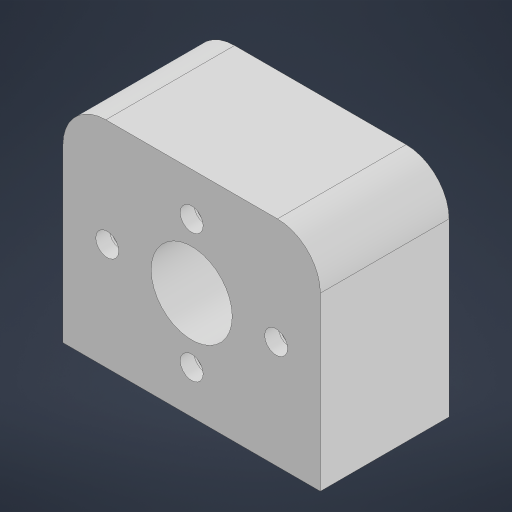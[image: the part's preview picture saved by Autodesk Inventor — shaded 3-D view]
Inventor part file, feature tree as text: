
AUTODESK INVENTOR PART (.ipt)
format: ipt  version: 2023 (Build 270158000, 158)  size: 222,720 bytes
history: native  units: in
note: dims shown in document units (in); Inventor stores cm internally (conversion verified against a paired STEP export)
features: sketch x5, hole x3, extrude x2, projected_geometry x2, chamfer x1, fillet x1
ambient origin geometry x8: Origin, YZ Plane, XZ Plane, XY Plane, X Axis, Y Axis, Z Axis, Center Point
bodies: Solid1 (feature_tree)
feature tree (14):
  extrude  "Extrusion1"  Depth=1.25in
  hole  "Hole1"  [1 undecoded]
  hole  "Hole2"  [1 undecoded]
  chamfer  "Chamfer1"  Distance=0.32in
  hole  "Hole3"  [1 undecoded]
  extrude  "Extrusion2"  Depth=0.25in
  fillet  "Fillet2"  Radius=1.0in
  sketch  "Sketch1"  dims[d0=1.5in d1=1.25in]
  sketch  "Sketch2"  dims[d2=0.75in d3=0.0in d4=0.9843in d5=0.748in d6=0.258in d7=0.251in]
  sketch  "Sketch3"  dims[d8=0.134in d9=0.75in d10=0.375in d11=0.25in d12=0.5635in d13=1.2625in d14=0.0in]
  projected_geometry  "Projected Loop1"
  sketch  "Sketch4"  dims[d15=0.24in d16=0.75in d17=0.375in d18=0.25in d19=0.5635in d20=0.63in d21=0.0in d22=0.04in d23=0.125in d24=45.0deg]
  projected_geometry  "Projected Loop2"
  sketch  "Sketch5"  dims[d25=0.375in d26=0.32in d27=0.28in d28=0.75in d29=0.375in d30=0.25in d31=0.5635in d32=0.41in d33=0.0in d34=0.4331in d35=0.4724in d36=1.0in d37=0.0in d39=0.25in]
note: 3 required parameter values undecoded (feature->parameter linkage not recoverable at this tier; creation-order binding heuristic only, values carry confidence <= 0.55)
